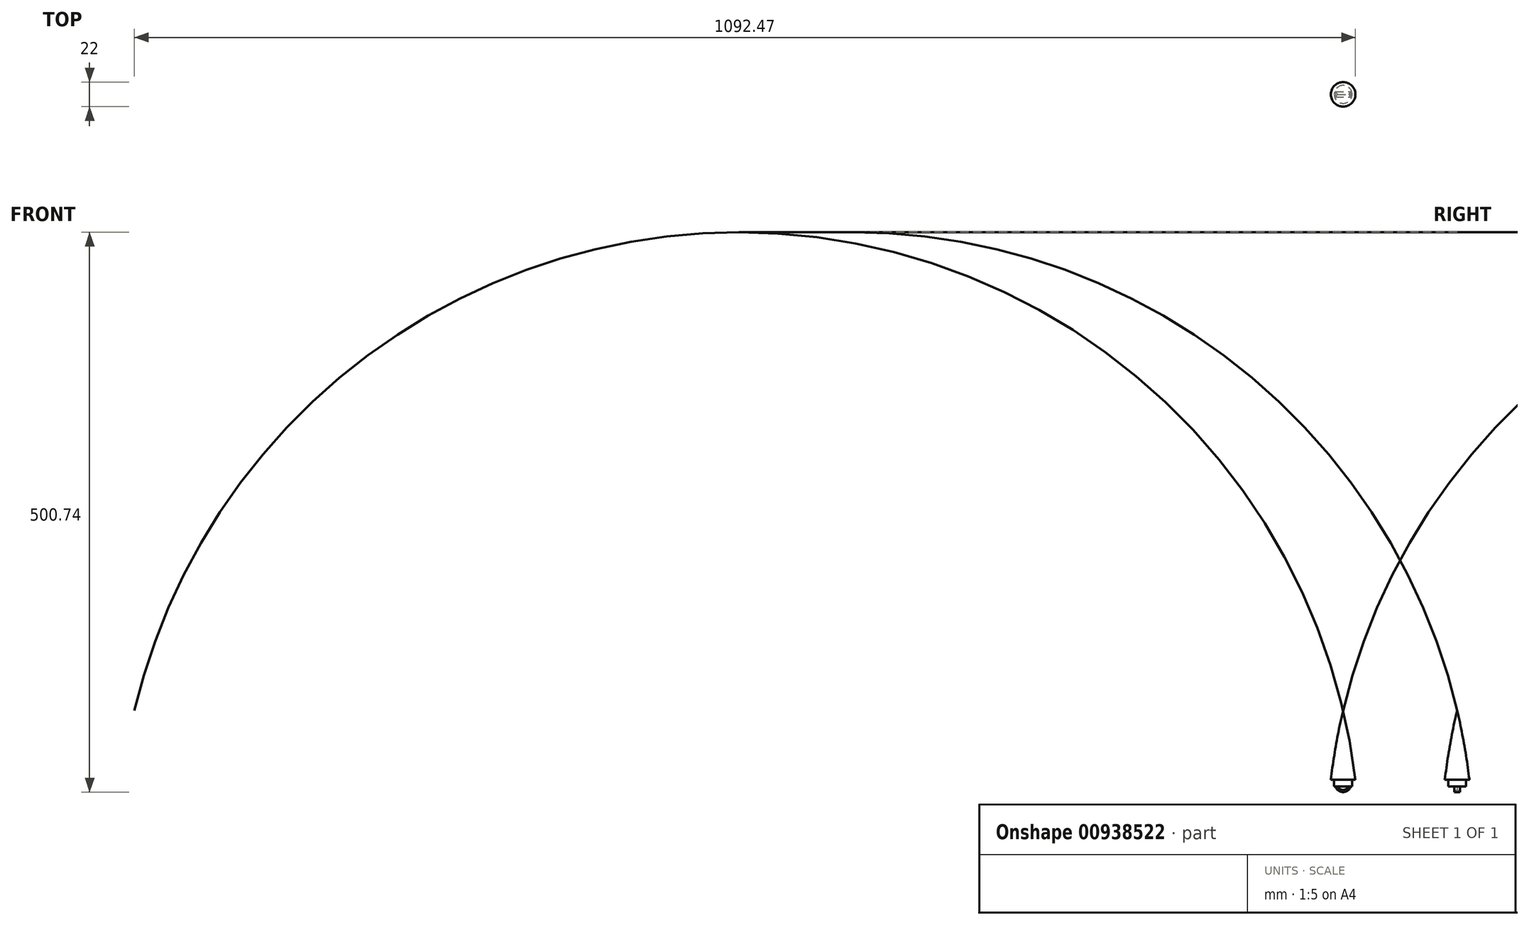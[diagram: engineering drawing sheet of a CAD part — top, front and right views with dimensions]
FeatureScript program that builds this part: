
annotation { "Feature Type Name" : "Feature", "Feature Type Description" : "" }
export const myFeature = defineFeature(function(context is Context, id is Id, definition is map)
    precondition{}
    {
        {
            var Q0;
            Q0=qCreatedBy(makeId("Front.planeOp"),FACE);
            var sketch = newSketch(context, id + "F0", { "sketchPlane" : qUnion([Q0])});
            skLineSegment(sketch, "E0", {"start": v(0, 0) * mm, "end": v(8, 0) * mm});
            skLineSegment(sketch, "E1", {"start": v(0, 0) * mm, "end": v(0, 68) * mm});
            skLineSegment(sketch, "E2", {"start": v(8, 0) * mm, "end": v(8, 6) * mm});
            skLineSegment(sketch, "E3", {"start": v(8, 6) * mm, "end": v(11, 6) * mm});
            skArc(sketch, "E4", {"start": v(11, 6) * mm, "mid": v(6.38, 37.16) * mm, "end": v(0, 68) * mm});
            skSolve(sketch);
        }
        {
            var Q0;
            Q0=makeQuery(id+"F0.imprint","IMPRINT",FACE,{"disambiguationData":[TD([[makeQuery(id+"F0.imprint","IMPRINT",EDGE,{"derivedFrom":sQuery(id+"F0.wireOp",EDGE,"E0")}),1.0]])]});
            var Q1;
            Q1=sQuery(id+"F0.wireOp",EDGE,"E1");
            revolve(context, id + "F1", {"surfaceOperationType" : NewSurfaceOperationType.NEW, "entities" : qUnion([Q0]), "axis" : qUnion([Q1]), "revolveType" : RevolveType.FULL});
        }
        {
            var Q0;
            Q0=qCreatedBy(makeId("Front.planeOp"),FACE);
            var sketch = newSketch(context, id + "F2", { "sketchPlane" : qUnion([Q0])});
            skArc(sketch, "E5", {"start": v(-6.93, 0) * mm, "mid": v(0, -5) * mm, "end": v(6.93, 0) * mm});
            skArc(sketch, "E6", {"start": v(-4.93, 0) * mm, "mid": v(0, -2.96) * mm, "end": v(4.93, 0) * mm});
            skLineSegment(sketch, "E7", {"start": v(-6.93, 0) * mm, "end": v(6.93, 0) * mm});
            skSolve(sketch);
        }
        {
            var Q0;
            {var subQ0=sQuery(id+"F2.wireOp",EDGE,"E5");Q0=makeQuery(id+"F2.imprint","IMPRINT",FACE,{"disambiguationData":[TD([[makeQuery(id+"F2.imprint","IMPRINT",EDGE,{"derivedFrom":subQ0}),1.0]])]});}
            extrude(context, id + "F3", {"entities" : qUnion([Q0]), "operationType" : NewBodyOperationType.ADD, "endBound" : BoundingType.SYMMETRIC, "depth" : 5 * mm, "offsetDistance" : 25 * mm});
        }
        {
            var Q0;
            Q0=makeQuery(id+"F3.opExtrude","CAP_EDGE",EDGE,{"disambiguationData":[OSD([sQuery(id+"F2.wireOp",EDGE,"E6")])],"isStart":false});
            var Q1;
            Q1=makeQuery(id+"F3.opExtrude","CAP_EDGE",EDGE,{"disambiguationData":[OSD([sQuery(id+"F2.wireOp",EDGE,"E6")])],"isStart":true});
            fillet(context, id + "F4", {"entities" : qUnion([Q0, Q1]), "radius" : 5 * mm, "tangentPropagation" : true, "allowEdgeOverflow" : false});
        }
    });
